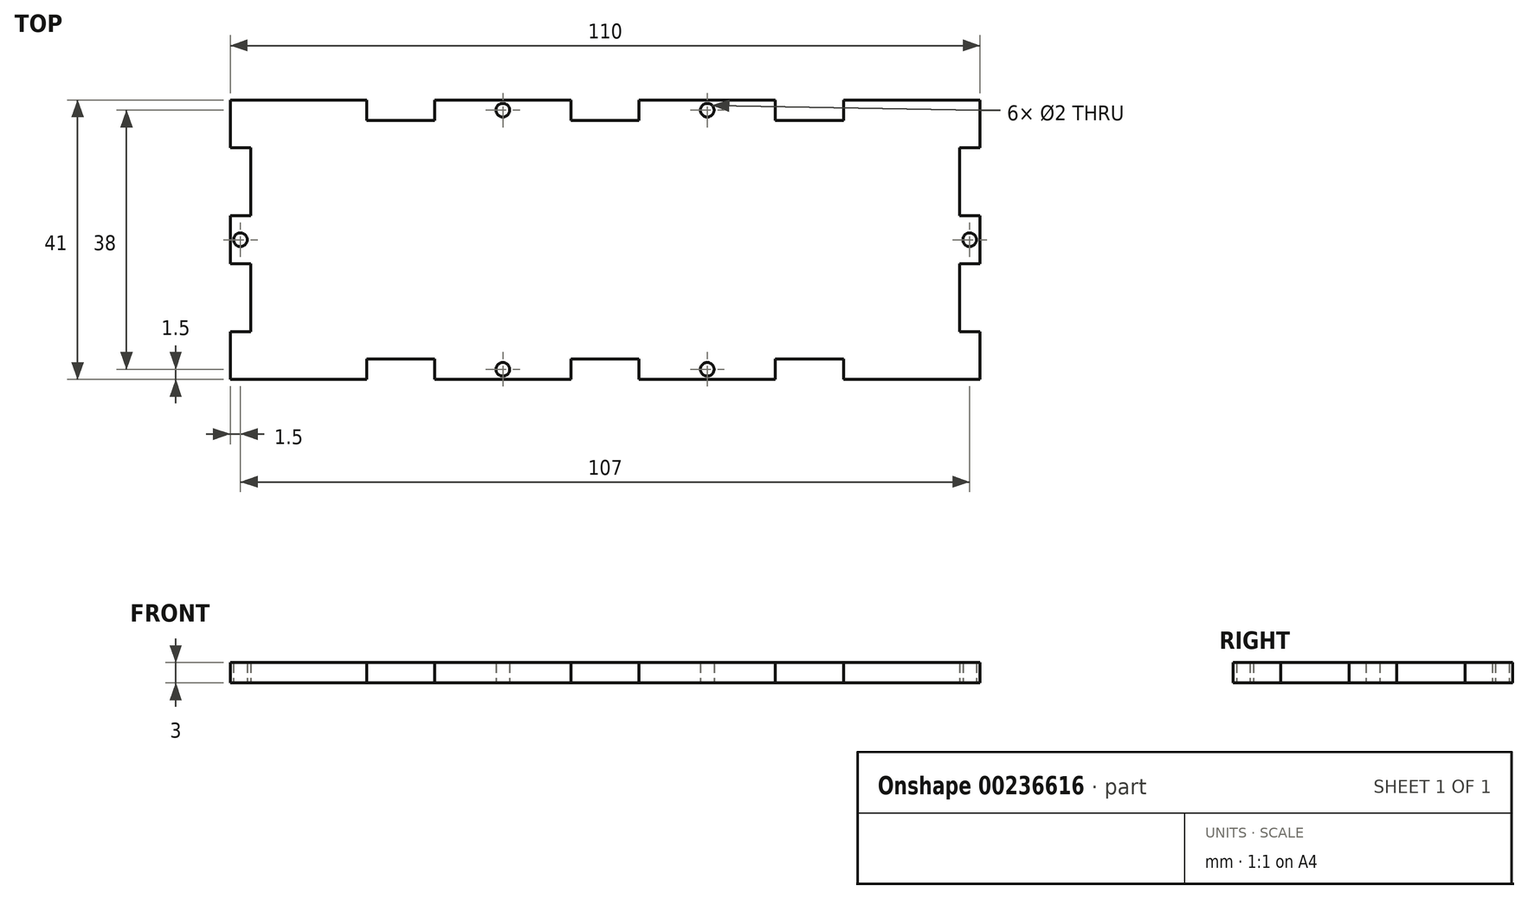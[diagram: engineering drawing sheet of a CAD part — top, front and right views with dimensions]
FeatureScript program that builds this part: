
annotation { "Feature Type Name" : "Feature", "Feature Type Description" : "" }
export const myFeature = defineFeature(function(context is Context, id is Id, definition is map)
    precondition{}
    {
        {
            var Q0;
            Q0=qCreatedBy(makeId("Top.planeOp"),FACE);
            var sketch = newSketch(context, id + "F0", { "sketchPlane" : qUnion([Q0])});
            skLineSegment(sketch, "E0", {"start": v(0, 0) * mm, "end": v(0, 7) * mm});
            skLineSegment(sketch, "E1", {"start": v(0, 7) * mm, "end": v(3, 7) * mm});
            skLineSegment(sketch, "E2", {"start": v(3, 7) * mm, "end": v(3, 17) * mm});
            skLineSegment(sketch, "E3", {"start": v(3, 17) * mm, "end": v(0, 17) * mm});
            skLineSegment(sketch, "E4", {"start": v(0, 17) * mm, "end": v(0, 24) * mm});
            skLineSegment(sketch, "E5", {"start": v(0, 24) * mm, "end": v(3, 24) * mm});
            skLineSegment(sketch, "E6", {"start": v(3, 24) * mm, "end": v(3, 34) * mm});
            skLineSegment(sketch, "E7", {"start": v(3, 34) * mm, "end": v(0, 34) * mm});
            skLineSegment(sketch, "E8", {"start": v(0, 34) * mm, "end": v(0, 41) * mm});
            skLineSegment(sketch, "E9", {"start": v(0, 0) * mm, "end": v(20, 0) * mm});
            skLineSegment(sketch, "E10", {"start": v(20, 0) * mm, "end": v(20, 3) * mm});
            skLineSegment(sketch, "E11", {"start": v(20, 3) * mm, "end": v(30, 3) * mm});
            skLineSegment(sketch, "E12", {"start": v(30, 3) * mm, "end": v(30, 0) * mm});
            skLineSegment(sketch, "E13", {"start": v(30, 0) * mm, "end": v(50, 0) * mm});
            skLineSegment(sketch, "E14", {"start": v(50, 0) * mm, "end": v(50, 3) * mm});
            skLineSegment(sketch, "E15", {"start": v(50, 3) * mm, "end": v(60, 3) * mm});
            skLineSegment(sketch, "E16", {"start": v(60, 0) * mm, "end": v(80, 0) * mm});
            skLineSegment(sketch, "E17", {"start": v(80, 0) * mm, "end": v(80, 3) * mm});
            skLineSegment(sketch, "E18", {"start": v(80, 3) * mm, "end": v(90, 3) * mm});
            skLineSegment(sketch, "E19", {"start": v(90, 3) * mm, "end": v(90, 0) * mm});
            skLineSegment(sketch, "E20", {"start": v(90, 0) * mm, "end": v(110, 0) * mm});
            skLineSegment(sketch, "E21", {"start": v(60, 3) * mm, "end": v(60, 0) * mm});
            skLineSegment(sketch, "E22", {"start": v(55, 3) * mm, "end": v(55, 34) * mm, "construction": true});
            skLineSegment(sketch, "E23.MirrorCS", {"start": v(107, 17) * mm, "end": v(110, 17) * mm});
            skLineSegment(sketch, "E24.MirrorCS", {"start": v(110, 24) * mm, "end": v(107, 24) * mm});
            skLineSegment(sketch, "E25.MirrorCS", {"start": v(110, 7) * mm, "end": v(107, 7) * mm});
            skLineSegment(sketch, "E26.MirrorCS", {"start": v(107, 34) * mm, "end": v(110, 34) * mm});
            skLineSegment(sketch, "E27.MirrorCS", {"start": v(107, 7) * mm, "end": v(107, 17) * mm});
            skLineSegment(sketch, "E28.MirrorCS", {"start": v(110, 17) * mm, "end": v(110, 24) * mm});
            skLineSegment(sketch, "E29.MirrorCS", {"start": v(110, 34) * mm, "end": v(110, 41) * mm});
            skLineSegment(sketch, "E30.MirrorCS", {"start": v(110, 0) * mm, "end": v(110, 7) * mm});
            skLineSegment(sketch, "E31.MirrorCS", {"start": v(107, 24) * mm, "end": v(107, 34) * mm});
            skLineSegment(sketch, "E32", {"start": v(0, 20.5) * mm, "end": v(124.38, 20.5) * mm, "construction": true});
            skPoint(sketch, "E32.endSnap0", {"position": v(110, 20.5) * mm});
            skLineSegment(sketch, "E33.MirrorCS", {"start": v(50, 41) * mm, "end": v(50, 38) * mm});
            skLineSegment(sketch, "E34.MirrorCS", {"start": v(60, 38) * mm, "end": v(60, 41) * mm});
            skLineSegment(sketch, "E35.MirrorCS", {"start": v(90, 38) * mm, "end": v(90, 41) * mm});
            skLineSegment(sketch, "E36.MirrorCS", {"start": v(30, 38) * mm, "end": v(30, 41) * mm});
            skLineSegment(sketch, "E37.MirrorCS", {"start": v(20, 41) * mm, "end": v(20, 38) * mm});
            skLineSegment(sketch, "E38.MirrorCS", {"start": v(80, 41) * mm, "end": v(80, 38) * mm});
            skLineSegment(sketch, "E39.MirrorCS", {"start": v(60, 41) * mm, "end": v(80, 41) * mm});
            skLineSegment(sketch, "E40.MirrorCS", {"start": v(80, 38) * mm, "end": v(90, 38) * mm});
            skLineSegment(sketch, "E41.MirrorCS", {"start": v(0, 41) * mm, "end": v(20, 41) * mm});
            skLineSegment(sketch, "E42.MirrorCS", {"start": v(90, 41) * mm, "end": v(110, 41) * mm});
            skLineSegment(sketch, "E43.MirrorCS", {"start": v(20, 38) * mm, "end": v(30, 38) * mm});
            skLineSegment(sketch, "E44.MirrorCS", {"start": v(50, 38) * mm, "end": v(60, 38) * mm});
            skLineSegment(sketch, "E45.MirrorCS", {"start": v(30, 41) * mm, "end": v(50, 41) * mm});
            skCircle(sketch, "E46", {"center": v(40, 1.5) * mm, "radius": 1 * mm});
            skPoint(sketch, "E46.centerSnap0", {"position": v(40, 0) * mm});
            skCircle(sketch, "E47.MirrorC", {"center": v(70, 1.5) * mm, "radius": 1 * mm});
            skCircle(sketch, "E48.MirrorC", {"center": v(70, 39.5) * mm, "radius": 1 * mm});
            skCircle(sketch, "E49.MirrorC", {"center": v(40, 39.5) * mm, "radius": 1 * mm});
            skCircle(sketch, "E50", {"center": v(1.5, 20.5) * mm, "radius": 1 * mm});
            skCircle(sketch, "E51.MirrorC", {"center": v(108.5, 20.5) * mm, "radius": 1 * mm});
            skLineSegment(sketch, "E52", {"start": v(25, 38) * mm, "end": v(25, 3) * mm, "construction": true});
            skPoint(sketch, "E53.centerSnap0", {"position": v(3, 29) * mm});
            skLineSegment(sketch, "E54", {"start": v(85, 38) * mm, "end": v(85, 3) * mm, "construction": true});
            skSolve(sketch);
        }
        {
            var Q0;
            Q0=qSketchRegion(id+"F0",true);
            extrude(context, id + "F1", {"entities" : qUnion([Q0]), "endBound" : BoundingType.SYMMETRIC, "depth" : 3 * mm});
        }
    });
